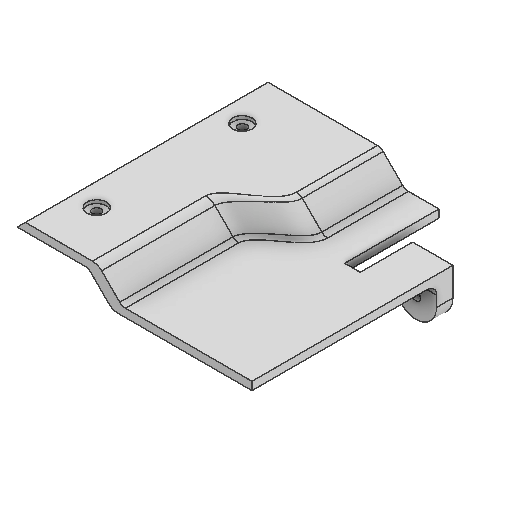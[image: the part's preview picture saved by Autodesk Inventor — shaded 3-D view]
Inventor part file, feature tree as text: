
AUTODESK INVENTOR PART (.ipt)
format: ipt  version: 2025 (Build 290162000, 162)  size: 408,576 bytes
history: native  units: mm
features: sketch x10, extrude x8, projected_geometry x8, plane x4, other x4, reference x3, fillet x1, loft x1
ambient origin geometry x8: Origin, YZ Plane, XZ Plane, XY Plane, X Axis, Y Axis, Z Axis, Center Point
bodies: Solid1 (feature_tree)
feature tree (39):
  extrude  "Extrusion1"  Depth=240.0mm TaperAngle=0.0deg
  sketch  "Sketch2"  dims[d4=10.0mm d5=0.0mm d6=10.0mm d7=0.0mm]
  plane  "Work Plane1"
  extrude  "Extrusion2"  Depth=10.0mm TaperAngle=0.0deg
  sketch  "Sketch3"  dims[d8=6.0mm d9=5.5mm]
  plane  "Work Plane2"
  extrude  "Extrusion3"  Depth=5.5mm
  extrude  "Extrusion4"  Depth=30.0mm
  fillet  "Fillet1"  Radius=30.0mm
  extrude  "Extrusion5"  Depth=12.0mm
  extrude  "Extrusion6"  Depth=2.0mm TaperAngle=0.0deg
  extrude  "Extrusion7"  Depth=30.0mm
  plane  "Work Plane3"
  sketch  "Sketch8"  dims[d22=5.0mm d23=8.0mm]
  sketch  "Sketch9"  dims[d35=10.0mm d36=90.0deg d37=10.0mm d38=90.0deg]
  plane  "Work Plane4"
  loft  "Loft2"
  extrude  "Extrusion9"  Depth=10.0mm TaperAngle=90.0deg
  sketch  "Sketch1"  dims[d0=150.0mm d1=0.0mm d2=240.0mm d3=0.0mm]
  reference  "Reference1"
  projected_geometry  "Projected Loop1"
  projected_geometry  "Projected Loop2"
  sketch  "Sketch4"  dims[d10=5.5mm d11=30.0mm d12=30.0mm]
  reference  "Reference2"
  projected_geometry  "Projected Loop3"
  sketch  "Sketch5"  dims[d13=0.0mm d14=0.0mm d15=12.0mm]
  reference  "Reference3"
  projected_geometry  "Projected Loop4"
  sketch  "Sketch6"  dims[d16=12.0mm d17=2.0mm d18=0.0mm]
  sketch  "Sketch7"  dims[d19=100.0mm d20=0.0mm d21=30.0mm]
  projected_geometry  "Projected Loop5"
  projected_geometry  "Projected Loop6"
  projected_geometry  "Projected Loop7"
  other  "Edges2"
  sketch  "Sketch11"  dims[d39=10.0mm d40=0.0mm]
  projected_geometry  "Projected Loop9"
  other  "<userpath>\Desktop\puppycat\woodhouseMK1.iam"
  other  "woodhouseMK1.iam"
  other  "frontLeftSidePlate:1"
